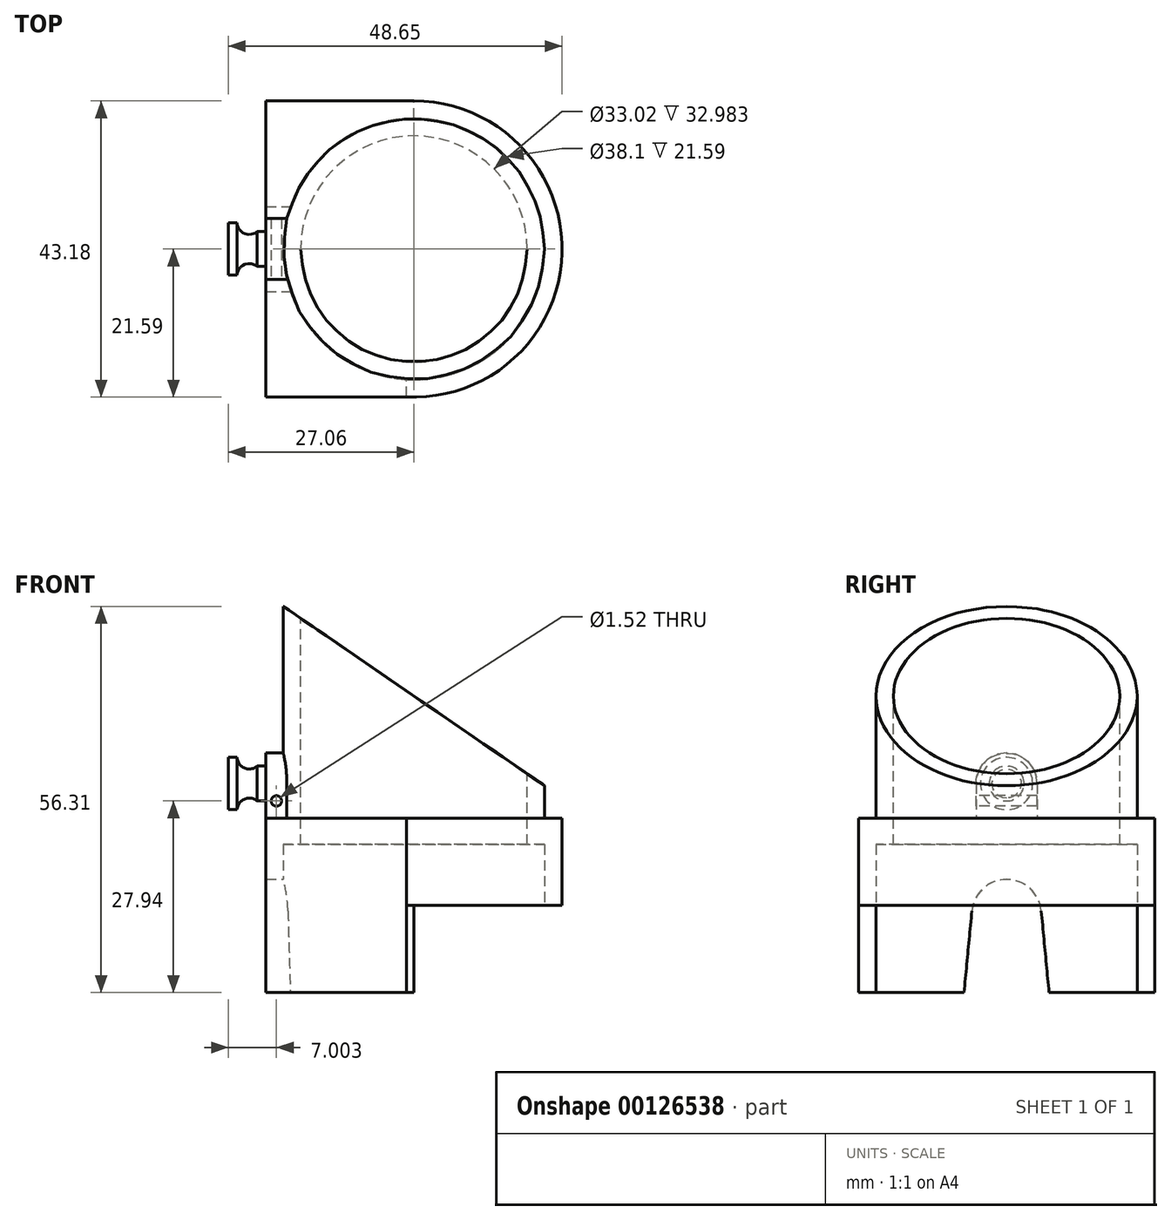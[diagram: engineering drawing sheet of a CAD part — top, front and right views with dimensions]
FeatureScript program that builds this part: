
annotation { "Feature Type Name" : "Feature", "Feature Type Description" : "" }
export const myFeature = defineFeature(function(context is Context, id is Id, definition is map)
    precondition{}
    {
        {
            var Q0;
            Q0=qCreatedBy(makeId("Top.planeOp"),FACE);
            var sketch = newSketch(context, id + "F0", { "sketchPlane" : qUnion([Q0])});
            skCircle(sketch, "E0", {"center": v(0, 0) * mm, "radius": 19.05 * mm});
            skCircle(sketch, "E1", {"center": v(0, 0) * mm, "radius": 21.59 * mm});
            skSolve(sketch);
        }
        {
            var Q0;
            Q0 = qSketchRegion(id + "F0", true);
            extrude(context, id + "F1", {"entities" : qUnion([Q0]), "depth" : 12.7 * mm});
        }
        {
            var Q0;
            Q0=makeQuery(id+"F1.opExtrude","CAP_FACE",FACE,{"disambiguationData":[OSD([sQuery(id+"F0.wireOp",EDGE,"E0"),sQuery(id+"F0.wireOp",EDGE,"E1")])],"isStart":false});
            var sketch = newSketch(context, id + "F2", { "sketchPlane" : qUnion([Q0])});
            skCircle(sketch, "E2", {"center": v(0, 0) * mm, "radius": 19.05 * mm});
            skCircle(sketch, "E3", {"center": v(0, 0) * mm, "radius": 16.51 * mm});
            skSolve(sketch);
        }
        {
            var Q0;
            Q0 = qSketchRegion(id + "F2", true);
            extrude(context, id + "F3", {"entities" : qUnion([Q0]), "operationType" : NewBodyOperationType.ADD, "oppositeDirection" : true, "depth" : 3.8 * mm});
        }
        {
            var Q0;
            Q0=makeQuery(id+"F3.boolean.opBoolean","MERGE",FACE,{"derivedFrom":[makeQuery(id+"F1.opExtrude","CAP_FACE",FACE,{"disambiguationData":[OSD([sQuery(id+"F0.wireOp",EDGE,"E0"),sQuery(id+"F0.wireOp",EDGE,"E1")])],"isStart":false}),makeQuery(id+"F3.opExtrude","CAP_FACE",FACE,{"disambiguationData":[OSD([sQuery(id+"F2.wireOp",EDGE,"E2"),sQuery(id+"F2.wireOp",EDGE,"E3")])],"isStart":true})]});
            var sketch = newSketch(context, id + "F4", { "sketchPlane" : qUnion([Q0])});
            skLineSegment(sketch, "E4", {"start": v(0, 19.05) * mm, "end": v(0, 21.59) * mm});
            skLineSegment(sketch, "E5", {"start": v(-21.6, 21.59) * mm, "end": v(0, 21.59) * mm});
            skLineSegment(sketch, "E6", {"start": v(-21.6, 21.59) * mm, "end": v(-21.59, -21.56) * mm});
            skLineSegment(sketch, "E7", {"start": v(-1.12, -21.56) * mm, "end": v(-21.6, -21.56) * mm});
            skLineSegment(sketch, "E8", {"start": v(-1.12, -21.56) * mm, "end": v(-1.12, -19.02) * mm});
            skLineSegment(sketch, "E9", {"start": v(0, 0) * mm, "end": v(-44.5, 0) * mm, "construction": true});
            skPoint(sketch, "E10", {"position": v(-21.59, 0) * mm});
            skArc(sketch, "E11", {"start": v(0, 19.05) * mm, "mid": v(-19.04, 0.56) * mm, "end": v(-1.12, -19.02) * mm});
            skSolve(sketch);
        }
        {
            var Q0;
            Q0 = qSketchRegion(id + "F4", true);
            extrude(context, id + "F5", {"entities" : qUnion([Q0]), "operationType" : NewBodyOperationType.ADD, "oppositeDirection" : true, "depth" : 25.4 * mm});
        }
        {
            var Q0;
            Q0=qCreatedBy(makeId("Right.planeOp"),FACE);
            var sketch = newSketch(context, id + "F6", { "sketchPlane" : qUnion([Q0])});
            skLineSegment(sketch, "E12", {"start": v(7.53, 0) * mm, "end": v(-6.4, 0) * mm});
            skLineSegment(sketch, "E13", {"start": v(0, -58.6) * mm, "end": v(0, 21.6) * mm, "construction": true});
            skLineSegment(sketch, "E14", {"start": v(0, 3.8) * mm, "end": v(0, 3.8) * mm});
            skLineSegment(sketch, "E15", {"start": v(-5.06, -0.79) * mm, "end": v(-6.48, -15.63) * mm});
            skLineSegment(sketch, "E16", {"start": v(-6.42, -18.5) * mm, "end": v(-5.04, -29.02) * mm});
            skPoint(sketch, "E16.endSnap0", {"position": v(0, -33.44) * mm});
            skLineSegment(sketch, "E17", {"start": v(0, -33.44) * mm, "end": v(0, -33.44) * mm});
            skPoint(sketch, "E18.visualSharp", {"position": v(-4.62, 3.81) * mm});
            skArc(sketch, "E18.filletArc", {"start": v(0, 3.81) * mm, "mid": v(-3.42, 2.49) * mm, "end": v(-5.06, -0.79) * mm});
            skPoint(sketch, "E19.visualSharp", {"position": v(-4.45, -33.44) * mm});
            skArc(sketch, "E19.filletArc", {"start": v(-5.04, -29.02) * mm, "mid": v(-3.35, -32.17) * mm, "end": v(0, -33.44) * mm});
            skPoint(sketch, "E20.visualSharp", {"position": v(-6.61, -17.06) * mm});
            skArc(sketch, "E20.filletArc", {"start": v(-6.48, -15.63) * mm, "mid": v(-6.53, -17.06) * mm, "end": v(-6.42, -18.5) * mm});
            skArc(sketch, "E21.MirrorCS", {"start": v(6.48, -15.63) * mm, "mid": v(6.53, -17.06) * mm, "end": v(6.42, -18.5) * mm});
            skArc(sketch, "E22.MirrorCS", {"start": v(0, 3.81) * mm, "mid": v(3.42, 2.49) * mm, "end": v(5.06, -0.79) * mm});
            skArc(sketch, "E23.MirrorCS", {"start": v(5.04, -29.02) * mm, "mid": v(3.35, -32.17) * mm, "end": v(0, -33.44) * mm});
            skLineSegment(sketch, "E24.MirrorCS", {"start": v(6.42, -18.5) * mm, "end": v(5.04, -29.02) * mm});
            skPoint(sketch, "E25.MirrorP", {"position": v(6.61, -17.06) * mm});
            skPoint(sketch, "E26.MirrorP", {"position": v(4.45, -33.44) * mm});
            skLineSegment(sketch, "E27.MirrorCS", {"start": v(5.06, -0.79) * mm, "end": v(6.48, -15.63) * mm});
            skPoint(sketch, "E28.MirrorP", {"position": v(4.62, 3.81) * mm});
            skSolve(sketch);
        }
        {
            var Q0;
            Q0 = qSketchRegion(id + "F6", true);
            extrude(context, id + "F7", {"entities" : qUnion([Q0]), "operationType" : NewBodyOperationType.REMOVE, "oppositeDirection" : true, "depth" : 25.4 * mm});
        }
        {
            var Q0;
            Q0=makeQuery(id+"F5.opExtrude","SWEPT_FACE",FACE,{"disambiguationData":[OSD([sQuery(id+"F4.wireOp",EDGE,"E6")])]});
            var sketch = newSketch(context, id + "F8", { "sketchPlane" : qUnion([Q0])});
            skLineSegment(sketch, "E29", {"start": v(-4.45, 12.7) * mm, "end": v(-4.45, 17.78) * mm});
            skLineSegment(sketch, "E30", {"start": v(4.45, 12.7) * mm, "end": v(4.45, 17.78) * mm});
            skArc(sketch, "E31", {"start": v(4.45, 17.78) * mm, "mid": v(0, 22.23) * mm, "end": v(-4.45, 17.78) * mm});
            skLineSegment(sketch, "E32", {"start": v(0, 0) * mm, "end": v(0, 26.73) * mm, "construction": true});
            skPoint(sketch, "E32.endSnap0", {"position": v(0, 3.81) * mm});
            skLineSegment(sketch, "E33", {"start": v(-4.45, 12.7) * mm, "end": v(4.45, 12.7) * mm});
            skSolve(sketch);
        }
        {
            var Q0;
            Q0 = qSketchRegion(id + "F8", true);
            extrude(context, id + "F9", {"entities" : qUnion([Q0]), "operationType" : NewBodyOperationType.ADD, "oppositeDirection" : true, "depth" : 5.08 * mm});
        }
        {
            var Q0;
            Q0=makeQuery(id+"F5.boolean.opBoolean","MERGE",FACE,{"derivedFrom":[makeQuery(id+"F3.boolean.opBoolean","MERGE",FACE,{"derivedFrom":[makeQuery(id+"F1.opExtrude","CAP_FACE",FACE,{"disambiguationData":[OSD([sQuery(id+"F0.wireOp",EDGE,"E0"),sQuery(id+"F0.wireOp",EDGE,"E1")])],"isStart":false}),makeQuery(id+"F3.opExtrude","CAP_FACE",FACE,{"disambiguationData":[OSD([sQuery(id+"F2.wireOp",EDGE,"E2"),sQuery(id+"F2.wireOp",EDGE,"E3")])],"isStart":true})]}),makeQuery(id+"F5.opExtrude","CAP_FACE",FACE,{"disambiguationData":[OSD([sQuery(id+"F4.wireOp",EDGE,"E4"),sQuery(id+"F4.wireOp",EDGE,"E5"),sQuery(id+"F4.wireOp",EDGE,"E6"),sQuery(id+"F4.wireOp",EDGE,"E7"),sQuery(id+"F4.wireOp",EDGE,"E8"),sQuery(id+"F4.wireOp",EDGE,"E11")])],"isStart":true})]});
            var sketch = newSketch(context, id + "F10", { "sketchPlane" : qUnion([Q0])});
            skCircle(sketch, "E34", {"center": v(0, 0) * mm, "radius": 19.05 * mm});
            skCircle(sketch, "E35", {"center": v(0, 0) * mm, "radius": 16.51 * mm});
            skSolve(sketch);
        }
        {
            var Q0;
            Q0 = qSketchRegion(id + "F10", true);
            extrude(context, id + "F11", {"entities" : qUnion([Q0]), "operationType" : NewBodyOperationType.ADD, "depth" : 31.75 * mm});
        }
        {
            var Q0;
            Q0=makeQuery(id+"F5.opExtrude","SWEPT_FACE",FACE,{"disambiguationData":[OSD([sQuery(id+"F4.wireOp",EDGE,"E7")])]});
            var sketch = newSketch(context, id + "F12", { "sketchPlane" : qUnion([Q0])});
            skLineSegment(sketch, "E36", {"start": v(19.46, 17.18) * mm, "end": v(-20.27, 44.45) * mm});
            skLineSegment(sketch, "E37", {"start": v(-20.27, 44.45) * mm, "end": v(19.46, 44.45) * mm});
            skLineSegment(sketch, "E38", {"start": v(19.46, 44.45) * mm, "end": v(19.46, 17.18) * mm});
            skSolve(sketch);
        }
        {
            var Q0;
            Q0 = qSketchRegion(id + "F12", true);
            extrude(context, id + "F13", {"entities" : qUnion([Q0]), "operationType" : NewBodyOperationType.REMOVE, "endBound" : BoundingType.THROUGH_ALL, "oppositeDirection" : true, "depth" : 25.4 * mm});
        }
        {
            var Q0;
            Q0=makeQuery(id+"F9.opExtrude","SWEPT_FACE",FACE,{"disambiguationData":[OSD([sQuery(id+"F8.wireOp",EDGE,"E30")])]});
            var sketch = newSketch(context, id + "F14", { "sketchPlane" : qUnion([Q0])});
            skCircle(sketch, "E39", {"center": v(-20.06, 15.24) * mm, "radius": 0.76 * mm});
            skPoint(sketch, "E39.centerSnap0", {"position": v(-20.06, 12.7) * mm});
            skPoint(sketch, "E39.centerSnap1", {"position": v(-21.59, 15.24) * mm});
            skSolve(sketch);
        }
        {
            var Q0;
            Q0 = qSketchRegion(id + "F14", true);
            extrude(context, id + "F15", {"entities" : qUnion([Q0]), "operationType" : NewBodyOperationType.REMOVE, "oppositeDirection" : true, "depth" : 25.4 * mm});
        }
        {
            var Q0;
            Q0=makeQuery(id+"F5.boolean.opBoolean","MERGE",FACE,{"derivedFrom":[makeQuery(id+"F3.boolean.opBoolean","MERGE",FACE,{"derivedFrom":[makeQuery(id+"F1.opExtrude","CAP_FACE",FACE,{"disambiguationData":[OSD([sQuery(id+"F0.wireOp",EDGE,"E0"),sQuery(id+"F0.wireOp",EDGE,"E1")])],"isStart":false}),makeQuery(id+"F3.opExtrude","CAP_FACE",FACE,{"disambiguationData":[OSD([sQuery(id+"F2.wireOp",EDGE,"E2"),sQuery(id+"F2.wireOp",EDGE,"E3")])],"isStart":true})]}),makeQuery(id+"F5.opExtrude","CAP_FACE",FACE,{"disambiguationData":[OSD([sQuery(id+"F4.wireOp",EDGE,"E4"),sQuery(id+"F4.wireOp",EDGE,"E5"),sQuery(id+"F4.wireOp",EDGE,"E6"),sQuery(id+"F4.wireOp",EDGE,"E7"),sQuery(id+"F4.wireOp",EDGE,"E8"),sQuery(id+"F4.wireOp",EDGE,"E11")])],"isStart":true})]});
            cPlane(context, id + "F16", {"entities" : qUnion([Q0]), "cplaneType" : CPlaneType.OFFSET, "offset" : 5.08 * mm, "width" : 152.4 * mm, "height" : 152.4 * mm});
        }
        {
            var Q0;
            Q0=qCreatedBy(id+"F16.planeOp",FACE);
            var sketch = newSketch(context, id + "F17", { "sketchPlane" : qUnion([Q0])});
            skLineSegment(sketch, "E40", {"start": v(0, 0) * mm, "end": v(-53.1, 0) * mm, "construction": true});
            skLineSegment(sketch, "E41", {"start": v(-21.59, 0) * mm, "end": v(-21.59, 2.54) * mm});
            skLineSegment(sketch, "E42", {"start": v(-21.59, 2.54) * mm, "end": v(-22.86, 2.54) * mm});
            skLineSegment(sketch, "E43", {"start": v(-27.06, 3.81) * mm, "end": v(-27.06, 0) * mm});
            skLineSegment(sketch, "E44", {"start": v(-27.06, 3.81) * mm, "end": v(-25.79, 3.81) * mm});
            skLineSegment(sketch, "E45", {"start": v(-21.59, 0) * mm, "end": v(-27.06, 0) * mm});
            skArc(sketch, "E46", {"start": v(-25.79, 3.81) * mm, "mid": v(-24.72, 2.27) * mm, "end": v(-22.86, 2.54) * mm});
            skSolve(sketch);
        }
        {
            var Q0;
            Q0 = qSketchRegion(id + "F17", true);
            var Q1;
            Q1=sQuery(id+"F17.wireOp",EDGE,"E40");
            revolve(context, id + "F18", {"operationType" : NewBodyOperationType.ADD, "entities" : qUnion([Q0]), "axis" : qUnion([Q1]), "revolveType" : RevolveType.FULL});
        }
    });
